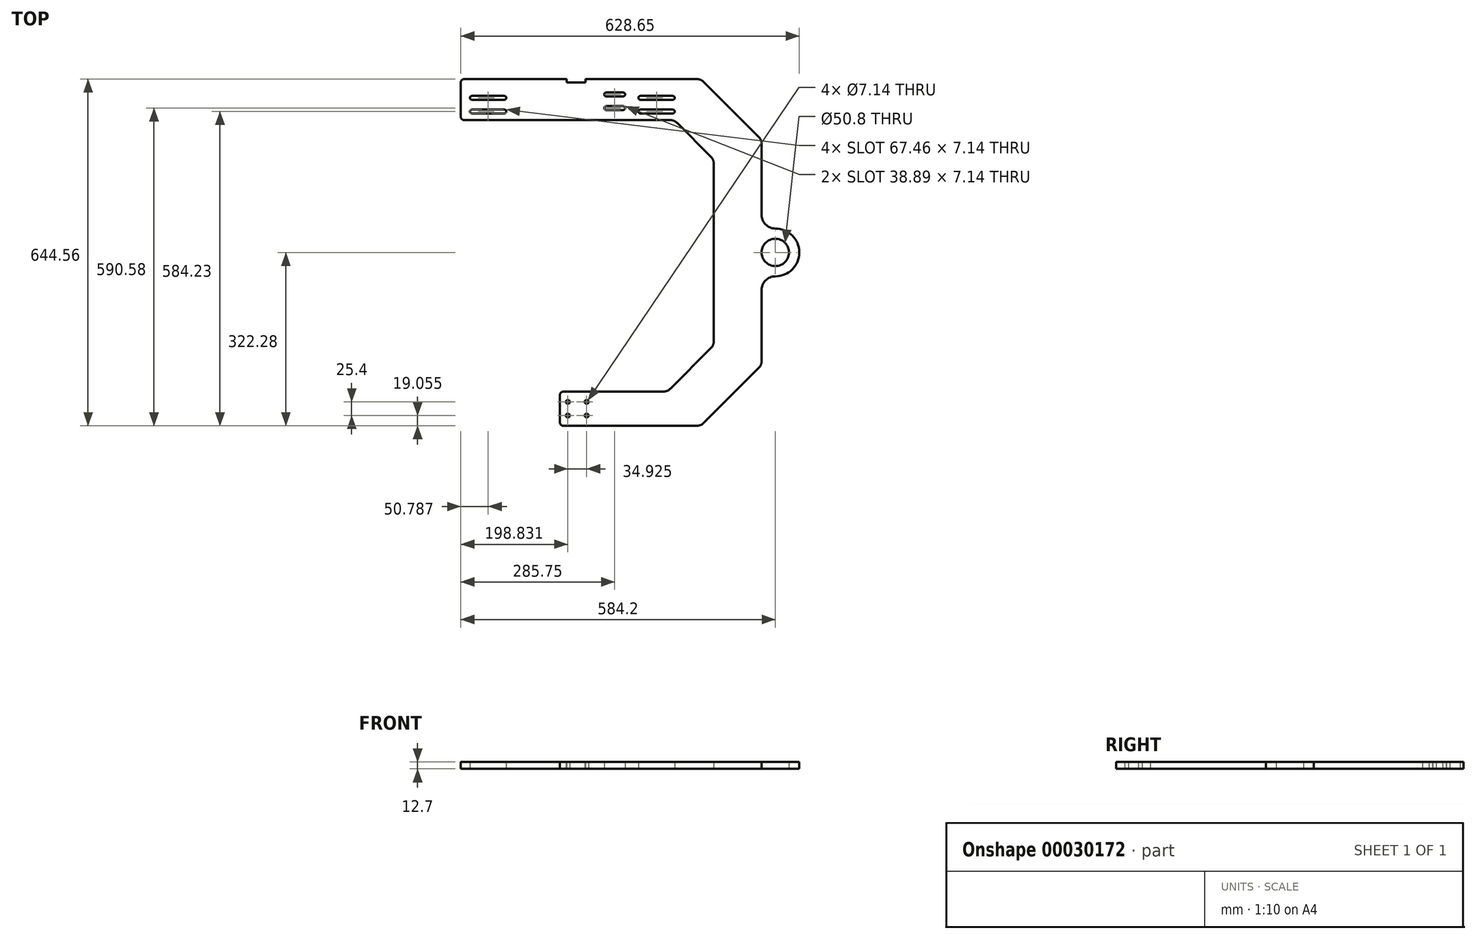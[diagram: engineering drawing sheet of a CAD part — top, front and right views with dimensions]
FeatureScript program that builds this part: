
annotation { "Feature Type Name" : "Feature", "Feature Type Description" : "" }
export const myFeature = defineFeature(function(context is Context, id is Id, definition is map)
    precondition{}
    {
        {
            var Q0;
            Q0=qCreatedBy(makeId("Top.planeOp"),FACE);
            var sketch = newSketch(context, id + "F0", { "sketchPlane" : qUnion([Q0])});
            skCircle(sketch, "E0", {"center": v(0, 0) * mm, "radius": 25.4 * mm});
            skArc(sketch, "E1.0", {"start": v(0, -44.45) * mm, "mid": v(44.45, 0) * mm, "end": v(0, 44.45) * mm});
            skLineSegment(sketch, "E2", {"start": v(-25.4, 44.45) * mm, "end": v(-25.4, 209.55) * mm});
            skLineSegment(sketch, "E3", {"start": v(-25.4, 209.55) * mm, "end": v(-138.13, 322.28) * mm});
            skLineSegment(sketch, "E4", {"start": v(-138.13, 322.28) * mm, "end": v(-352.43, 322.28) * mm});
            skLineSegment(sketch, "E5", {"start": v(-584.2, 322.28) * mm, "end": v(-584.2, 246.08) * mm});
            skLineSegment(sketch, "E6", {"start": v(-584.2, 246.08) * mm, "end": v(-187.65, 246.08) * mm});
            skLineSegment(sketch, "E7", {"start": v(-187.65, 246.08) * mm, "end": v(-114.3, 172.73) * mm});
            skLineSegment(sketch, "E8", {"start": v(-114.3, 172.73) * mm, "end": v(-114.3, -172.73) * mm});
            skLineSegment(sketch, "E9", {"start": v(-200.35, -258.78) * mm, "end": v(-400.05, -258.78) * mm});
            skLineSegment(sketch, "E10", {"start": v(-400.05, -258.78) * mm, "end": v(-400.05, -322.28) * mm});
            skLineSegment(sketch, "E11", {"start": v(-400.05, -322.28) * mm, "end": v(-138.13, -322.28) * mm});
            skLineSegment(sketch, "E12", {"start": v(-25.4, -209.55) * mm, "end": v(-25.4, -44.45) * mm});
            skLineSegment(sketch, "E13.0", {"start": v(-200.35, -258.78) * mm, "end": v(-114.3, -172.73) * mm});
            skLineSegment(sketch, "E14", {"start": v(0, 44.45) * mm, "end": v(-25.4, 44.45) * mm});
            skLineSegment(sketch, "E15", {"start": v(0, -44.45) * mm, "end": v(-25.4, -44.45) * mm});
            skPoint(sketch, "E16.orphan", {"position": v(-44.45, 0) * mm});
            skLineSegment(sketch, "E17", {"start": v(-25.4, -209.55) * mm, "end": v(-138.13, -322.28) * mm});
            skCircle(sketch, "E18", {"center": v(-385.37, -303.23) * mm, "radius": 3.57 * mm});
            skCircle(sketch, "E19.0.1.0", {"center": v(-385.37, -277.83) * mm, "radius": 3.57 * mm});
            skCircle(sketch, "E19.1.0.0", {"center": v(-350.44, -303.23) * mm, "radius": 3.57 * mm});
            skCircle(sketch, "E19.1.1.0", {"center": v(-350.44, -277.83) * mm, "radius": 3.57 * mm});
            skLineSegment(sketch, "E19.direction1", {"start": v(-385.37, -303.23) * mm, "end": v(-350.44, -303.23) * mm, "construction": true});
            skLineSegment(sketch, "E19.direction2", {"start": v(-385.37, -303.23) * mm, "end": v(-385.37, -277.83) * mm, "construction": true});
            skArc(sketch, "E20.0.startCap", {"start": v(-563.58, 258.38) * mm, "mid": v(-567.14, 261.95) * mm, "end": v(-563.58, 265.52) * mm});
            skArc(sketch, "E20.0.endCap", {"start": v(-503.25, 265.52) * mm, "mid": v(-499.68, 261.95) * mm, "end": v(-503.25, 258.38) * mm});
            skLineSegment(sketch, "E20.0.left", {"start": v(-563.58, 265.52) * mm, "end": v(-503.25, 265.52) * mm});
            skLineSegment(sketch, "E20.0.right", {"start": v(-563.58, 258.38) * mm, "end": v(-503.25, 258.38) * mm});
            skArc(sketch, "E20.1.startCap", {"start": v(-314.33, 264.73) * mm, "mid": v(-317.9, 268.3) * mm, "end": v(-314.33, 271.87) * mm});
            skArc(sketch, "E20.1.endCap", {"start": v(-282.58, 271.87) * mm, "mid": v(-279, 268.3) * mm, "end": v(-282.58, 264.73) * mm});
            skLineSegment(sketch, "E20.1.left", {"start": v(-314.33, 271.87) * mm, "end": v(-282.58, 271.87) * mm});
            skLineSegment(sketch, "E20.1.right", {"start": v(-314.33, 264.73) * mm, "end": v(-282.58, 264.73) * mm});
            skArc(sketch, "E20.2.startCap", {"start": v(-250.83, 258.38) * mm, "mid": v(-254.4, 261.95) * mm, "end": v(-250.83, 265.52) * mm});
            skArc(sketch, "E20.2.endCap", {"start": v(-190.5, 265.52) * mm, "mid": v(-186.93, 261.95) * mm, "end": v(-190.5, 258.38) * mm});
            skLineSegment(sketch, "E20.2.left", {"start": v(-250.83, 265.52) * mm, "end": v(-190.5, 265.52) * mm});
            skLineSegment(sketch, "E20.2.right", {"start": v(-250.83, 258.38) * mm, "end": v(-190.5, 258.38) * mm});
            skLineSegment(sketch, "E21.0.1.0", {"start": v(-250.83, 290.92) * mm, "end": v(-190.5, 290.92) * mm});
            skLineSegment(sketch, "E21.0.1.1", {"start": v(-563.58, 290.92) * mm, "end": v(-503.25, 290.92) * mm});
            skLineSegment(sketch, "E21.0.1.2", {"start": v(-314.33, 290.13) * mm, "end": v(-282.58, 290.13) * mm});
            skLineSegment(sketch, "E21.0.1.3", {"start": v(-250.83, 283.78) * mm, "end": v(-190.5, 283.78) * mm});
            skLineSegment(sketch, "E21.0.1.4", {"start": v(-563.58, 283.78) * mm, "end": v(-503.25, 283.78) * mm});
            skLineSegment(sketch, "E21.0.1.5", {"start": v(-314.33, 297.27) * mm, "end": v(-282.58, 297.27) * mm});
            skArc(sketch, "E21.0.1.6", {"start": v(-282.58, 297.27) * mm, "mid": v(-279, 293.7) * mm, "end": v(-282.58, 290.13) * mm});
            skArc(sketch, "E21.0.1.7", {"start": v(-250.83, 283.78) * mm, "mid": v(-254.4, 287.35) * mm, "end": v(-250.83, 290.92) * mm});
            skArc(sketch, "E21.0.1.8", {"start": v(-503.25, 290.92) * mm, "mid": v(-499.68, 287.35) * mm, "end": v(-503.25, 283.78) * mm});
            skArc(sketch, "E21.0.1.9", {"start": v(-314.33, 290.13) * mm, "mid": v(-317.9, 293.7) * mm, "end": v(-314.33, 297.27) * mm});
            skArc(sketch, "E21.0.1.10", {"start": v(-563.58, 283.78) * mm, "mid": v(-567.14, 287.35) * mm, "end": v(-563.58, 290.92) * mm});
            skArc(sketch, "E21.0.1.11", {"start": v(-190.5, 290.92) * mm, "mid": v(-186.93, 287.35) * mm, "end": v(-190.5, 283.78) * mm});
            skLineSegment(sketch, "E21.direction1", {"start": v(-250.83, 265.52) * mm, "end": v(-225.43, 265.52) * mm, "construction": true});
            skLineSegment(sketch, "E21.direction2", {"start": v(-250.83, 265.52) * mm, "end": v(-250.83, 290.92) * mm, "construction": true});
            skLineSegment(sketch, "E22.0", {"start": v(-387.35, 322.28) * mm, "end": v(-387.35, 315.93) * mm});
            skLineSegment(sketch, "E23.0", {"start": v(-352.43, 315.93) * mm, "end": v(-387.35, 315.93) * mm});
            skLineSegment(sketch, "E24.0", {"start": v(-352.43, 322.28) * mm, "end": v(-352.43, 315.93) * mm});
            skLineSegment(sketch, "E25.trimOffspring", {"start": v(-387.35, 322.28) * mm, "end": v(-584.2, 322.28) * mm});
            skSolve(sketch);
        }
        {
            var Q0;
            Q0=makeQuery(id+"F0.imprint","IMPRINT",FACE,{"disambiguationData":[TD([[makeQuery(id+"F0.imprint","IMPRINT",EDGE,{"derivedFrom":sQuery(id+"F0.wireOp",EDGE,"E0")}),-1.0]])]});
            extrude(context, id + "F1", {"entities" : qUnion([Q0]), "depth" : 12.7 * mm});
        }
        {
            var Q0;
            Q0=makeQuery(id+"F1.opExtrude","SWEPT_EDGE",EDGE,{"disambiguationData":[OSD([sQuery(id+"F0.wireOp",EDGE,"E12"),sQuery(id+"F0.wireOp",EDGE,"E15")])]});
            var Q1;
            Q1=makeQuery(id+"F1.opExtrude","SWEPT_EDGE",EDGE,{"disambiguationData":[OSD([sQuery(id+"F0.wireOp",EDGE,"E2"),sQuery(id+"F0.wireOp",EDGE,"E14")])]});
            fillet(context, id + "F2", {"entities" : qUnion([Q0, Q1]), "radius" : 25.4 * mm, "tangentPropagation" : true, "allowEdgeOverflow" : false});
        }
        {
            var Q0;
            Q0=makeQuery(id+"F1.opExtrude","SWEPT_EDGE",EDGE,{"disambiguationData":[OSD([sQuery(id+"F0.wireOp",EDGE,"E12"),sQuery(id+"F0.wireOp",EDGE,"E17")])]});
            var Q1;
            Q1=makeQuery(id+"F1.opExtrude","SWEPT_EDGE",EDGE,{"disambiguationData":[OSD([sQuery(id+"F0.wireOp",EDGE,"E11"),sQuery(id+"F0.wireOp",EDGE,"E17")])]});
            var Q2;
            Q2=makeQuery(id+"F1.opExtrude","SWEPT_EDGE",EDGE,{"disambiguationData":[OSD([sQuery(id+"F0.wireOp",EDGE,"E2"),sQuery(id+"F0.wireOp",EDGE,"E3")])]});
            var Q3;
            Q3=makeQuery(id+"F1.opExtrude","SWEPT_EDGE",EDGE,{"disambiguationData":[OSD([sQuery(id+"F0.wireOp",EDGE,"E3"),sQuery(id+"F0.wireOp",EDGE,"E4")])]});
            var Q4;
            Q4=makeQuery(id+"F1.opExtrude","SWEPT_EDGE",EDGE,{"disambiguationData":[OSD([sQuery(id+"F0.wireOp",EDGE,"E7"),sQuery(id+"F0.wireOp",EDGE,"E8")])]});
            var Q5;
            Q5=makeQuery(id+"F1.opExtrude","SWEPT_EDGE",EDGE,{"disambiguationData":[OSD([sQuery(id+"F0.wireOp",EDGE,"E6"),sQuery(id+"F0.wireOp",EDGE,"E7")])]});
            var Q6;
            Q6=makeQuery(id+"F1.opExtrude","SWEPT_EDGE",EDGE,{"disambiguationData":[OSD([sQuery(id+"F0.wireOp",EDGE,"E8"),sQuery(id+"F0.wireOp",EDGE,"E13.0")])]});
            var Q7;
            Q7=makeQuery(id+"F1.opExtrude","SWEPT_EDGE",EDGE,{"disambiguationData":[OSD([sQuery(id+"F0.wireOp",EDGE,"E9"),sQuery(id+"F0.wireOp",EDGE,"E13.0")])]});
            fillet(context, id + "F3", {"entities" : qUnion([Q0, Q1, Q2, Q3, Q4, Q5, Q6, Q7]), "radius" : 19.05 * mm, "tangentPropagation" : true, "allowEdgeOverflow" : false});
        }
        {
            var Q0;
            Q0=makeQuery(id+"F1.opExtrude","SWEPT_EDGE",EDGE,{"disambiguationData":[OSD([sQuery(id+"F0.wireOp",EDGE,"E9"),sQuery(id+"F0.wireOp",EDGE,"E10")])]});
            var Q1;
            Q1=makeQuery(id+"F1.opExtrude","SWEPT_EDGE",EDGE,{"disambiguationData":[OSD([sQuery(id+"F0.wireOp",EDGE,"E10"),sQuery(id+"F0.wireOp",EDGE,"E11")])]});
            var Q2;
            Q2=makeQuery(id+"F1.opExtrude","SWEPT_EDGE",EDGE,{"disambiguationData":[OSD([sQuery(id+"F0.wireOp",EDGE,"E5"),sQuery(id+"F0.wireOp",EDGE,"E6")])]});
            var Q3;
            Q3=makeQuery(id+"F1.opExtrude","SWEPT_EDGE",EDGE,{"disambiguationData":[OSD([sQuery(id+"F0.wireOp",EDGE,"E5"),sQuery(id+"F0.wireOp",EDGE,"E25.trimOffspring")])]});
            fillet(context, id + "F4", {"entities" : qUnion([Q0, Q1, Q2, Q3]), "radius" : 6.35 * mm, "tangentPropagation" : true, "allowEdgeOverflow" : false});
        }
    });
